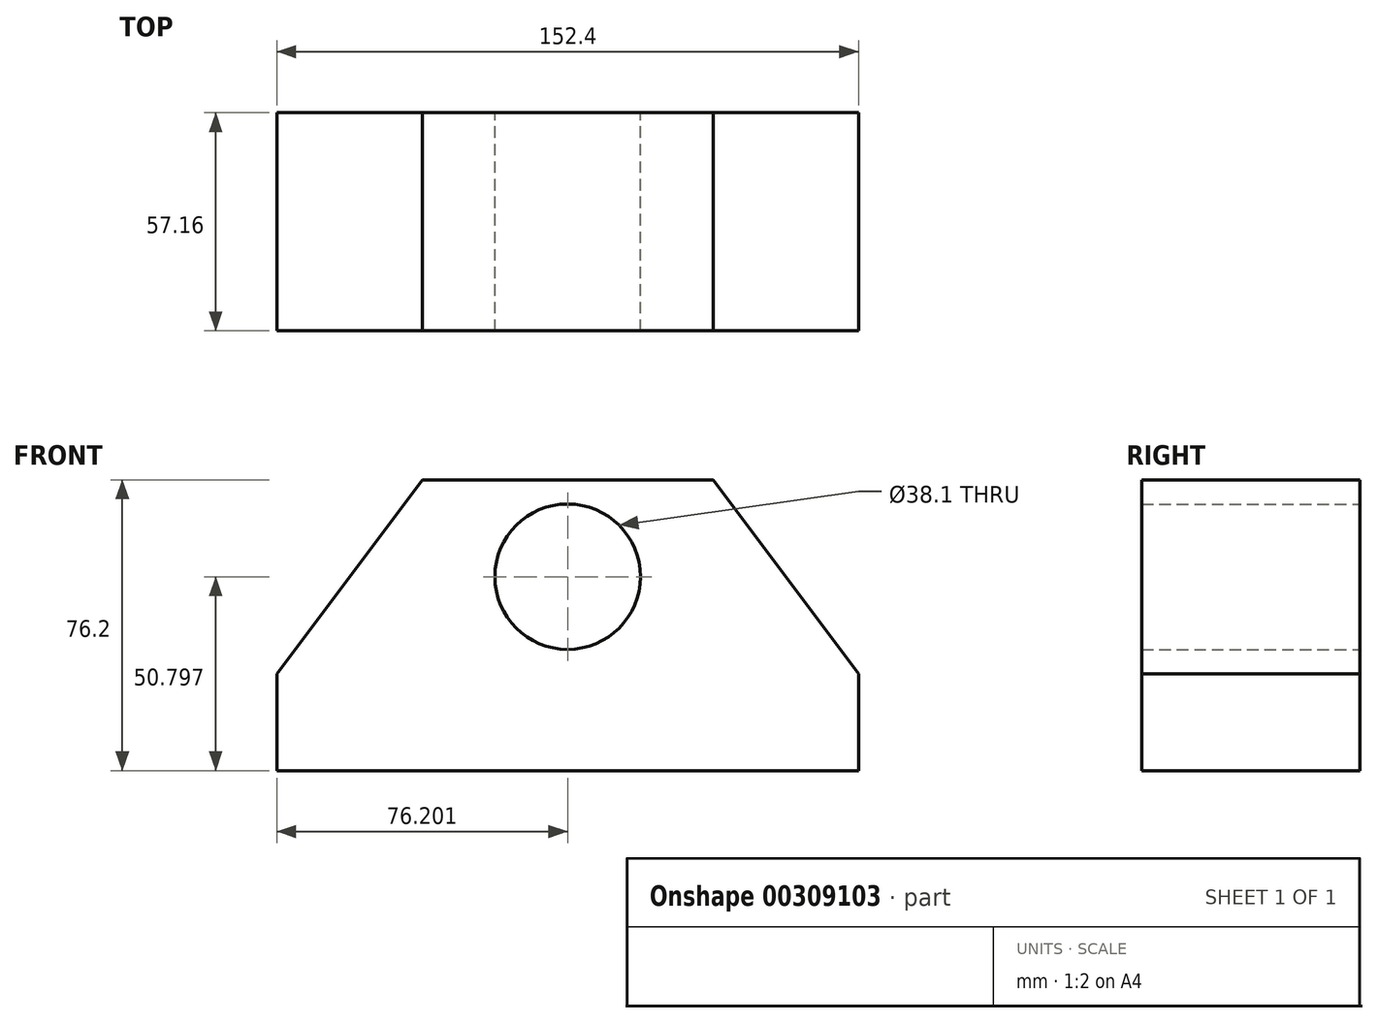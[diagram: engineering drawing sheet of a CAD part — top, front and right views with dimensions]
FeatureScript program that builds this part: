
annotation { "Feature Type Name" : "Feature", "Feature Type Description" : "" }
export const myFeature = defineFeature(function(context is Context, id is Id, definition is map)
    precondition{}
    {
        {
            var Q0;
            Q0=qCreatedBy(makeId("Front.planeOp"),FACE);
            var sketch = newSketch(context, id + "F0", { "sketchPlane" : qUnion([Q0])});
            skLineSegment(sketch, "E0", {"start": v(-35.69, -58.46) * mm, "end": v(116.71, -58.46) * mm});
            skLineSegment(sketch, "E1", {"start": v(116.71, -58.46) * mm, "end": v(116.71, -33.06) * mm});
            skLineSegment(sketch, "E2", {"start": v(116.71, -33.06) * mm, "end": v(78.61, 17.74) * mm});
            skLineSegment(sketch, "E3", {"start": v(78.61, 17.74) * mm, "end": v(2.41, 17.74) * mm});
            skLineSegment(sketch, "E4", {"start": v(2.41, 17.74) * mm, "end": v(-35.69, -33.06) * mm});
            skLineSegment(sketch, "E5", {"start": v(-35.69, -33.06) * mm, "end": v(-35.69, -58.46) * mm});
            skCircle(sketch, "E6", {"center": v(40.51, -7.66) * mm, "radius": 19.05 * mm});
            skSolve(sketch);
        }
        {
            var Q0;
            Q0=makeQuery(id+"F0.imprint","IMPRINT",FACE,{"disambiguationData":[TD([[makeQuery(id+"F0.imprint","IMPRINT",EDGE,{"derivedFrom":sQuery(id+"F0.wireOp",EDGE,"E0")}),1.0]])]});
            extrude(context, id + "F1", {"entities" : qUnion([Q0]), "depth" : 57.15 * mm, "symmetric" : true});
        }
    });
